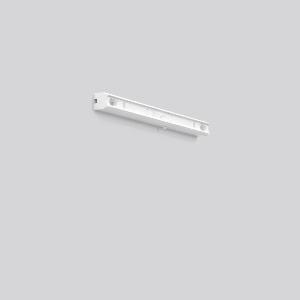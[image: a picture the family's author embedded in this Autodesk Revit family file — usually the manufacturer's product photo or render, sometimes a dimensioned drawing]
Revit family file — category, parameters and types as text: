
# Revit family: alu-stableuchten_41511_002_867e
name_source: partatom
category: Lighting Fixtures
units: mm (PartAtom-declared; Revit-internal decimal feet)

## family parameters
Cut with Voids When Loaded = No
Host = Face
Light Source = No
Part Type = Normal
Room Calculation Point = No
Round Connector Dimension = Use Diameter
Shared = No

## types (1)
- ALU-Stableuchten (1 x LED L S14S, 1000 lm, 16 W, 2700)
    Apparent Load = 16 VA
    CIE Flux Codes = 34 61 82 75 81
    Color Rendering = 80
    Color Temperature = 2700
    Default Elevation = 1800 mm
    Description = Series: Aluminium striplights
Aluminium striplight for linear lamps. Base: aluminium extrusion profile, powder-coated. End caps: plastic. With push button switch. Lamp contacts disconnection during lamp replacement. Light source must be ordered separately. 
Colour: white
Length: 500 mm
Width: 35 mm
Height: 58 mm
Lamp: L-DE
Number of lamps: 1
Wattage: 60 W
Socket: S14s
System power: 30 W
Rated luminous flux: 1100 lm
Luminous efficiency: 37 lm/W
Control gear: Converter not necessary
Protection class: I
Type of protection: IP 40
    Height = 58 mm
    Lamp = 1 x LED L S14S
    Lamp Light Flux = 1000 lm
    Lamp Power = 16 W
    Lamp count = 1
    Length = 500 mm
    Lifetime = 25000 h
    Luminous efficacy = 51 lm/W
    Manufacturer = RZB
    ModVariant = No
    Model = 41511.002
    Mounting Place = Ceiling, Wall
    Mounting Type = Surface mounted
    Number of Poles = 1
    OnlyDefault = Yes
    Power Factor = 1
    Product Name = ALU-Stableuchten
    Product group = Surface mounted ceiling and wall luminaires
    ProductGroupID = 305
    Protection Class = Protection class I
    Protection Degree = IP 40
    RLX_Detail_Level = 1
    RLX_Emergency_Light_Flux = 0 lm
    RLX_Emergency_Type = 0
    RLX_Emergency_Type_DB = No
    RlxData = <blob elided: 12181 chars, md5=fabb052d>
    Socket = S14s
    Standby Power = 0 W
    System Light Flux = 813 lm
    System Power = 16 W
    Type Comments = Product without accessories
    Type Image = 41511.002.jpg
    URL = http://relux.com
    VarID = ---
    Voltage = 230 V
    Voltage Range = 220-240 V
    Weight = 0.00 kg
    Width = 35 mm

## geometry (parser evidence)
native form markers: Sweep x10
no freeform markers — native parametric forms only
